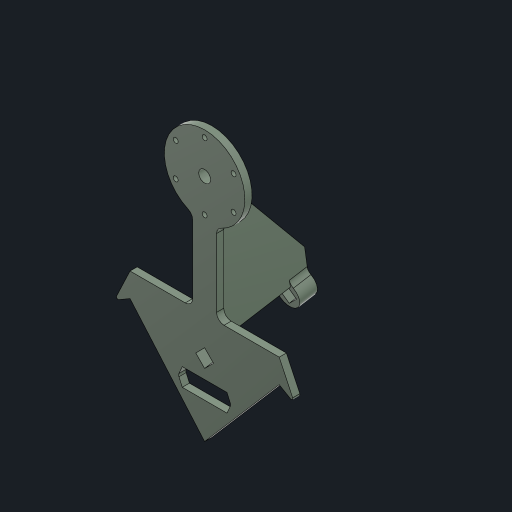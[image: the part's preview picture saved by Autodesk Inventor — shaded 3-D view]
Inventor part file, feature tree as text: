
AUTODESK INVENTOR PART (.ipt)
format: ipt  version: 2023 (Build 270158000, 158)  size: 399,360 bytes
history: native  units: mm
features: extrude x15, sketch x14, other x4, projected_geometry x2, mirror x1, hole x1, pattern_circular x1, fillet x1
ambient origin geometry x8: Origin, YZ Plane, XZ Plane, XY Plane, X Axis, Y Axis, Z Axis, Center Point
bodies: Body1 (feature_tree)
feature tree (39):
  other  "ソリッド1"
  sketch  "スケッチ1"
  extrude  "押し出し1"  Depth=2.4mm
  extrude  "押し出し2"  Depth=40.0mm
  extrude  "押し出し4"  Depth=14.3117mm
  extrude  "押し出し5"  Depth=8.0mm
  extrude  "爪"  Depth=180.0mm
  extrude  "押し出し17"  Depth=15.0mm
  extrude  "押し出し20"  Depth=14.0499mm
  extrude  "押し出し21"  Depth=30.0mm
  mirror  "ミラー1"
  extrude  "押し出し6"  Depth=25.0mm TaperAngle=0.0deg
  other  "作業平面2"
  extrude  "押し出し10"  Depth=4.0mm TaperAngle=0.0deg
  extrude  "ロッド穴"  Depth=1.4mm TaperAngle=0.0deg
  other  "作業平面3"
  extrude  "押し出し11"  TaperAngle=0.0deg  [1 undecoded]
  hole  "穴1"  [1 undecoded]
  pattern_circular  "円形状パターン1"  [2 undecoded]
  extrude  "穴延長"  Depth=1.4mm TaperAngle=0.0deg
  extrude  "押し出し12"  Depth=1.0mm
  extrude  "押し出し13"  Depth=4.2mm
  fillet  "フィレット2"  [1 undecoded]
  sketch  "スケッチ2"
  sketch  "スケッチ3"
  other  "作業平面1"
  sketch  "スケッチ6"
  sketch  "スケッチ7"
  sketch  "スケッチ8"
  projected_geometry  "投影ループ1"
  sketch  "スケッチ9"
  sketch  "スケッチ10"
  sketch  "スケッチ11"
  sketch  "スケッチ15"
  sketch  "スケッチ16"
  sketch  "スケッチ19"
  sketch  "スケッチ21"
  sketch  "スケッチ22"
  projected_geometry  "投影ループ2"
note: 5 required parameter values undecoded (feature->parameter linkage not recoverable at this tier; creation-order binding heuristic only, values carry confidence <= 0.55)
